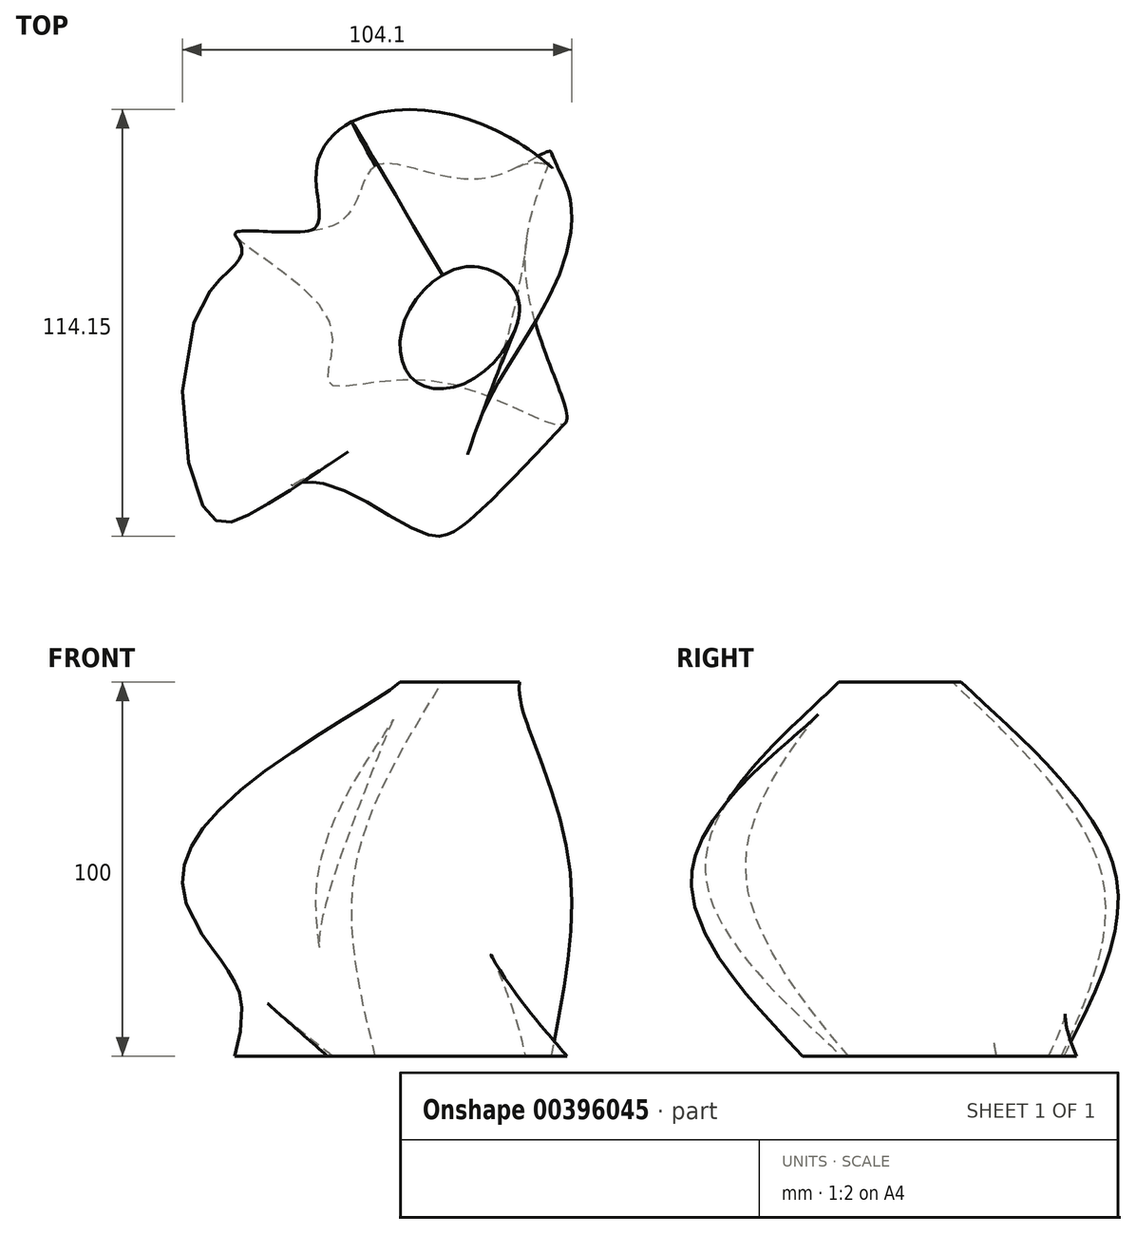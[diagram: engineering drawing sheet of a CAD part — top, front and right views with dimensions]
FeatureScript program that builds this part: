
annotation { "Feature Type Name" : "Feature", "Feature Type Description" : "" }
export const myFeature = defineFeature(function(context is Context, id is Id, definition is map)
    precondition{}
    {
        {
            var Q0;
            Q0=qCreatedBy(makeId("Top.planeOp"),FACE);
            var sketch = newSketch(context, id + "F0", { "sketchPlane" : qUnion([Q0])});
            skFitSpline(sketch, "E0", {"points": [v(-16.42, 36.36) * mm, v(-26.77, 20.94) * mm, v(-53.95, 18.38) * mm, v(-29.17, -4.28) * mm, v(-28.93, -21.5) * mm, v(0, -21.08) * mm, v(34.4, -32.45) * mm, v(23.66, 10.13) * mm, v(30.5, 40.27) * mm, v(11.65, 32.94) * mm, v(-16.42, 36.36) * mm]});
            skSolve(sketch);
        }
        {
            var Q0;
            Q0=qCreatedBy(makeId("Top.planeOp"),FACE);
            cPlane(context, id + "F1", {"entities" : qUnion([Q0]), "cplaneType" : CPlaneType.OFFSET, "offset" : 50 * mm, "width" : 152.4 * mm, "height" : 152.4 * mm});
        }
        {
            var Q0;
            Q0=qCreatedBy(makeId("Top.planeOp"),FACE);
            cPlane(context, id + "F2", {"entities" : qUnion([Q0]), "cplaneType" : CPlaneType.OFFSET, "offset" : 100 * mm, "width" : 152.4 * mm, "height" : 152.4 * mm});
        }
        {
            var Q0;
            Q0=qCreatedBy(id+"F1.planeOp",FACE);
            var sketch = newSketch(context, id + "F3", { "sketchPlane" : qUnion([Q0])});
            skFitSpline(sketch, "E1", {"points": [v(-27.73, 8.58) * mm, v(-60.42, 0) * mm, v(-58.77, -58.44) * mm, v(-35.4, -48.15) * mm, v(0, -62.36) * mm, v(11.56, -31.59) * mm, v(35.5, 21.5) * mm, v(0, 50.16) * mm, v(-31.33, 35.27) * mm, v(-27.73, 8.58) * mm]});
            skSolve(sketch);
        }
        {
            var Q0;
            Q0=qCreatedBy(id+"F2.planeOp",FACE);
            var sketch = newSketch(context, id + "F4", { "sketchPlane" : qUnion([Q0])});
            skFitSpline(sketch, "E2", {"points": [v(-8.68, -5.13) * mm, v(-6.25, -20.72) * mm, v(9.41, -20.75) * mm, v(21.98, 0) * mm, v(8.24, 9.5) * mm, v(-8.68, -5.13) * mm]});
            skSolve(sketch);
        }
        {
            var Q0;
            Q0=makeQuery(id+"F0.imprint","IMPRINT",FACE,{"disambiguationData":[TD([[makeQuery(id+"F0.imprint","IMPRINT",EDGE,{"derivedFrom":sQuery(id+"F0.wireOp",EDGE,"E0")}),1.0]])]});
            var Q1;
            Q1=makeQuery(id+"F3.imprint","IMPRINT",FACE,{"disambiguationData":[TD([[makeQuery(id+"F3.imprint","IMPRINT",EDGE,{"derivedFrom":sQuery(id+"F3.wireOp",EDGE,"E1")}),1.0]])]});
            var Q2;
            Q2=makeQuery(id+"F4.imprint","IMPRINT",FACE,{"disambiguationData":[TD([[makeQuery(id+"F4.imprint","IMPRINT",EDGE,{"derivedFrom":sQuery(id+"F4.wireOp",EDGE,"E2")}),1.0]])]});
            loft(context, id + "F5", {"sheetProfilesArray" : [{ "sheetProfileEntities" : qUnion([Q0]) }, { "sheetProfileEntities" : qUnion([Q1]) }, { "sheetProfileEntities" : qUnion([Q2]) }]});
        }
    });
